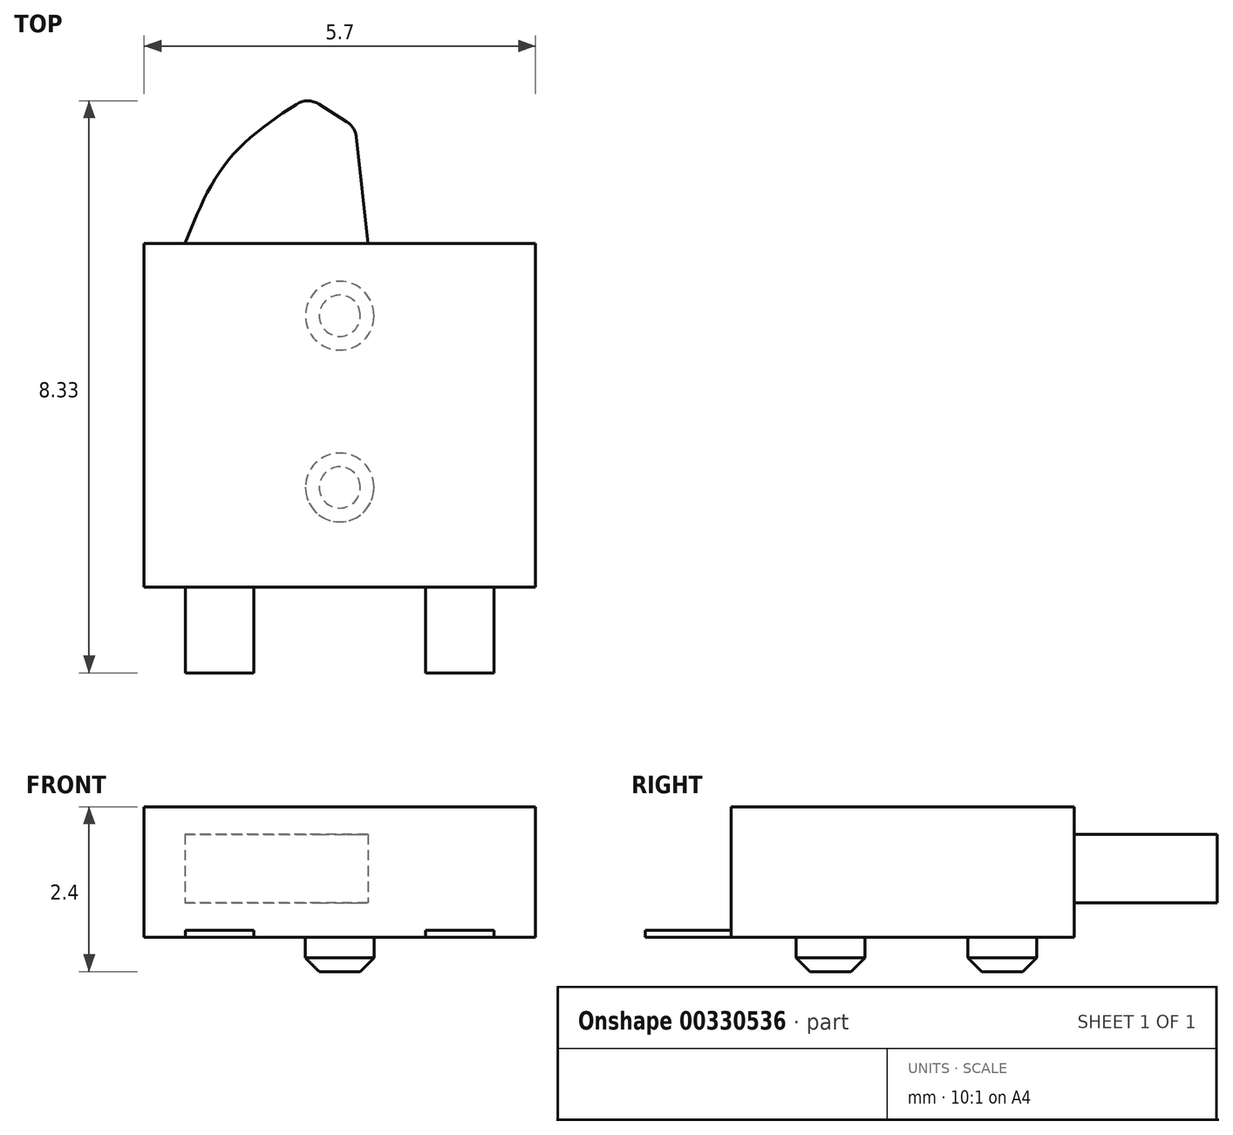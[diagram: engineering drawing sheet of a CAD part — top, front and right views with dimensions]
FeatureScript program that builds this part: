
annotation { "Feature Type Name" : "Feature", "Feature Type Description" : "" }
export const myFeature = defineFeature(function(context is Context, id is Id, definition is map)
    precondition{}
    {
        {
            var Q0;
            Q0=qCreatedBy(makeId("Top.planeOp"),FACE);
            var sketch = newSketch(context, id + "F0", { "sketchPlane" : qUnion([Q0])});
            skLineSegment(sketch, "E0.bottom", {"start": v(2.85, -2.5) * mm, "end": v(-2.85, -2.5) * mm});
            skLineSegment(sketch, "E0.top", {"start": v(2.85, 2.5) * mm, "end": v(-2.85, 2.5) * mm});
            skLineSegment(sketch, "E0.left", {"start": v(2.85, -2.5) * mm, "end": v(2.85, 2.5) * mm});
            skLineSegment(sketch, "E0.right", {"start": v(-2.85, -2.5) * mm, "end": v(-2.85, 2.5) * mm});
            skPoint(sketch, "E0.middle", {"position": v(0, 0) * mm});
            skSolve(sketch);
        }
        {
            var Q0;
            Q0 = qSketchRegion(id + "F0", true);
            extrude(context, id + "F1", {"entities" : qUnion([Q0]), "depth" : 1.9 * mm, "offsetDistance" : 25 * mm});
        }
        {
            var Q0;
            Q0=makeQuery(id+"F1.opExtrude","CAP_FACE",FACE,{"disambiguationData":[OSD([sQuery(id+"F0.wireOp",EDGE,"E0.bottom"),sQuery(id+"F0.wireOp",EDGE,"E0.top"),sQuery(id+"F0.wireOp",EDGE,"E0.left"),sQuery(id+"F0.wireOp",EDGE,"E0.right")])],"isStart":true});
            cPlane(context, id + "F2", {"entities" : qUnion([Q0]), "cplaneType" : CPlaneType.OFFSET, "offset" : 0.5 * mm, "oppositeDirection" : true, "width" : 150 * mm, "height" : 150 * mm});
        }
        {
            var Q0;
            Q0=qCreatedBy(id+"F2.planeOp",FACE);
            var sketch = newSketch(context, id + "F3", { "sketchPlane" : qUnion([Q0])});
            skLineSegment(sketch, "E1", {"start": v(-0.47, -4.63) * mm, "end": v(0.23, -4.2) * mm});
            skLineSegment(sketch, "E2", {"start": v(0.23, -4.2) * mm, "end": v(0.4, -2.5) * mm});
            skLineSegment(sketch, "E3", {"start": v(0.4, -2.5) * mm, "end": v(-2.25, -2.5) * mm});
            skFitSpline(sketch, "E4", {"points": [v(-2.25, -2.5) * mm, v(-1.61, -3.73) * mm, v(-0.47, -4.63) * mm], "startDerivative": vector(1.07, -2.67) * mm, "endDerivative": vector(2.5, -1.6) * mm});
            skSolve(sketch);
        }
        {
            var Q0;
            Q0 = qSketchRegion(id + "F3", true);
            extrude(context, id + "F4", {"entities" : qUnion([Q0]), "oppositeDirection" : true, "depth" : 1 * mm, "offsetDistance" : 25 * mm});
        }
        {
            var Q0;
            Q0=makeQuery(id+"F4.opExtrude","SWEPT_EDGE",EDGE,{"disambiguationData":[OSD([sQuery(id+"F3.wireOp",EDGE,"E1"),sQuery(id+"F3.wireOp",EDGE,"E4")])]});
            var Q1;
            Q1=makeQuery(id+"F4.opExtrude","SWEPT_EDGE",EDGE,{"disambiguationData":[OSD([sQuery(id+"F3.wireOp",EDGE,"E1"),sQuery(id+"F3.wireOp",EDGE,"E2")])]});
            fillet(context, id + "F5", {"entities" : qUnion([Q0, Q1]), "radius" : .3 * mm, "tangentPropagation" : true, "allowEdgeOverflow" : false});
        }
        {
            var Q0;
            Q0=makeQuery(id+"F1.opExtrude","CAP_FACE",FACE,{"disambiguationData":[OSD([sQuery(id+"F0.wireOp",EDGE,"E0.bottom"),sQuery(id+"F0.wireOp",EDGE,"E0.top"),sQuery(id+"F0.wireOp",EDGE,"E0.left"),sQuery(id+"F0.wireOp",EDGE,"E0.right")])],"isStart":true});
            var sketch = newSketch(context, id + "F6", { "sketchPlane" : qUnion([Q0])});
            skLineSegment(sketch, "E5", {"start": v(0, -2.5) * mm, "end": v(0, 2.5) * mm, "construction": true});
            skCircle(sketch, "E6", {"center": v(0, -1.45) * mm, "radius": 0.5 * mm});
            skCircle(sketch, "E7", {"center": v(0, 1.05) * mm, "radius": 0.5 * mm});
            skSolve(sketch);
        }
        {
            var Q0;
            Q0 = qSketchRegion(id + "F6", true);
            extrude(context, id + "F7", {"entities" : qUnion([Q0]), "operationType" : NewBodyOperationType.ADD, "depth" : 0.5 * mm, "offsetDistance" : 25 * mm});
        }
        {
            var Q0;
            Q0=makeQuery(id+"F7.opExtrude","CAP_EDGE",EDGE,{"disambiguationData":[OSD([sQuery(id+"F6.wireOp",EDGE,"E6")])],"isStart":false});
            var Q1;
            Q1=makeQuery(id+"F7.opExtrude","CAP_EDGE",EDGE,{"disambiguationData":[OSD([sQuery(id+"F6.wireOp",EDGE,"E7")])],"isStart":false});
            chamfer(context, id + "F8", {"entities" : qUnion([Q0, Q1]), "width" : .2 * mm, "tangentPropagation" : true});
        }
        {
            var Q0;
            Q0=makeQuery(id+"F1.opExtrude","CAP_FACE",FACE,{"disambiguationData":[OSD([sQuery(id+"F0.wireOp",EDGE,"E0.bottom"),sQuery(id+"F0.wireOp",EDGE,"E0.top"),sQuery(id+"F0.wireOp",EDGE,"E0.left"),sQuery(id+"F0.wireOp",EDGE,"E0.right")])],"isStart":true});
            var sketch = newSketch(context, id + "F9", { "sketchPlane" : qUnion([Q0])});
            skLineSegment(sketch, "E8", {"start": v(0, 0) * mm, "end": v(0, 3.73) * mm, "construction": true});
            skLineSegment(sketch, "E9.bottom", {"start": v(1.25, 3.75) * mm, "end": v(2.25, 3.75) * mm});
            skLineSegment(sketch, "E9.top", {"start": v(1.25, 2.5) * mm, "end": v(2.25, 2.5) * mm});
            skLineSegment(sketch, "E9.left", {"start": v(1.25, 3.75) * mm, "end": v(1.25, 2.5) * mm});
            skLineSegment(sketch, "E9.right", {"start": v(2.25, 3.75) * mm, "end": v(2.25, 2.5) * mm});
            skPoint(sketch, "E9.middle", {"position": v(1.75, 3.12) * mm});
            skLineSegment(sketch, "E10.MirrorCS", {"start": v(-1.25, 3.75) * mm, "end": v(-1.25, 2.5) * mm});
            skPoint(sketch, "E11.MirrorP", {"position": v(-1.75, 3.12) * mm});
            skLineSegment(sketch, "E12.MirrorCS", {"start": v(-1.25, 3.75) * mm, "end": v(-2.25, 3.75) * mm});
            skLineSegment(sketch, "E13.MirrorCS", {"start": v(-2.25, 3.75) * mm, "end": v(-2.25, 2.5) * mm});
            skLineSegment(sketch, "E14.MirrorCS", {"start": v(-1.25, 2.5) * mm, "end": v(-2.25, 2.5) * mm});
            skSolve(sketch);
        }
        {
            var Q0;
            Q0 = qSketchRegion(id + "F9", true);
            extrude(context, id + "F10", {"entities" : qUnion([Q0]), "operationType" : NewBodyOperationType.ADD, "oppositeDirection" : true, "depth" : .1 * mm, "offsetDistance" : 25 * mm});
        }
    });
